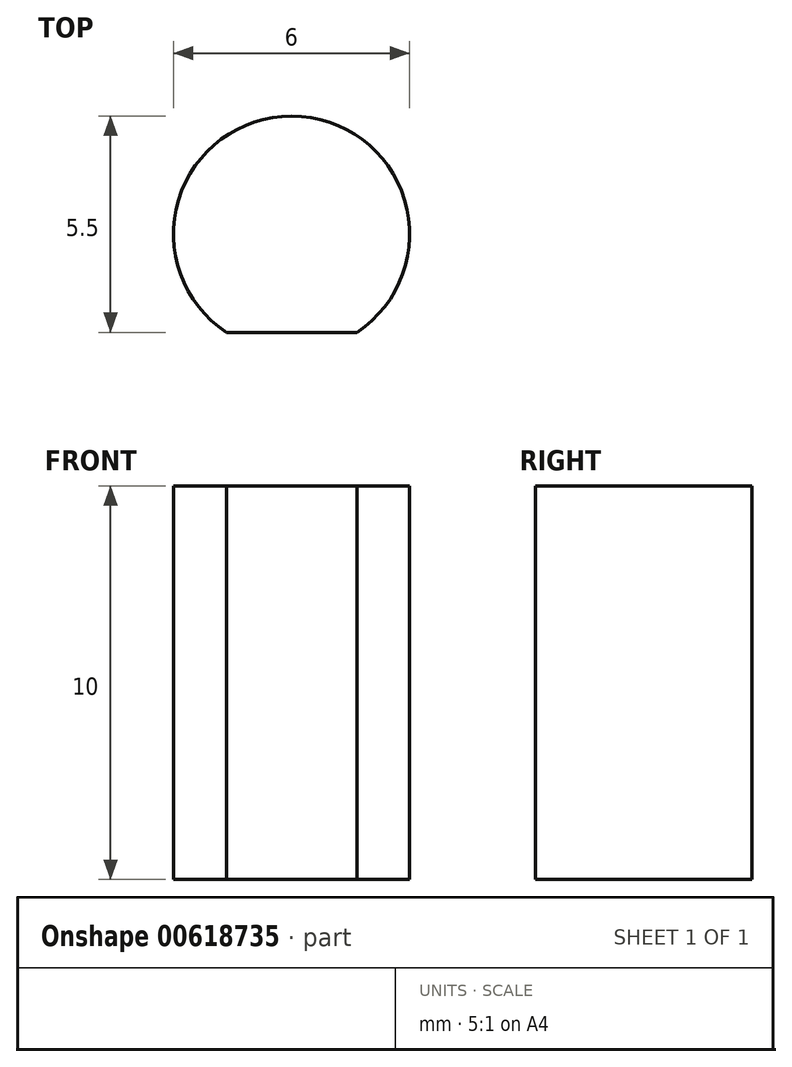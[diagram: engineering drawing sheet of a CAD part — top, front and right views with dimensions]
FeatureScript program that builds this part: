
annotation { "Feature Type Name" : "Feature", "Feature Type Description" : "" }
export const myFeature = defineFeature(function(context is Context, id is Id, definition is map)
    precondition{}
    {
        {
            var Q0;
            Q0=qCreatedBy(makeId("Top.planeOp"),FACE);
            var sketch = newSketch(context, id + "F0", { "sketchPlane" : qUnion([Q0])});
            skLineSegment(sketch, "E0", {"start": v(0, -2.5) * mm, "end": v(-1.66, -2.5) * mm});
            skLineSegment(sketch, "E1", {"start": v(-1.66, -2.5) * mm, "end": v(1.66, -2.5) * mm});
            skArc(sketch, "E2", {"start": v(-1.66, -2.5) * mm, "mid": v(0, 3) * mm, "end": v(1.66, -2.5) * mm});
            skArc(sketch, "E3.0", {"start": v(-3.32, -5) * mm, "mid": v(0, 6) * mm, "end": v(3.32, -5) * mm});
            skLineSegment(sketch, "E4", {"start": v(-3.32, -5) * mm, "end": v(3.32, -5) * mm});
            skSolve(sketch);
        }
        {
            var Q0;
            {var subQ0=sQuery(id+"F0.wireOp",EDGE,"E2");Q0=makeQuery(id+"F0.imprint","IMPRINT",FACE,{"disambiguationData":[TD([[makeQuery(id+"F0.imprint","IMPRINT",EDGE,{"derivedFrom":subQ0}),1.0]])]});}
            extrude(context, id + "F1", {"entities" : qUnion([Q0]), "depth" : 10 * mm, "offsetDistance" : 25 * mm});
        }
    });
